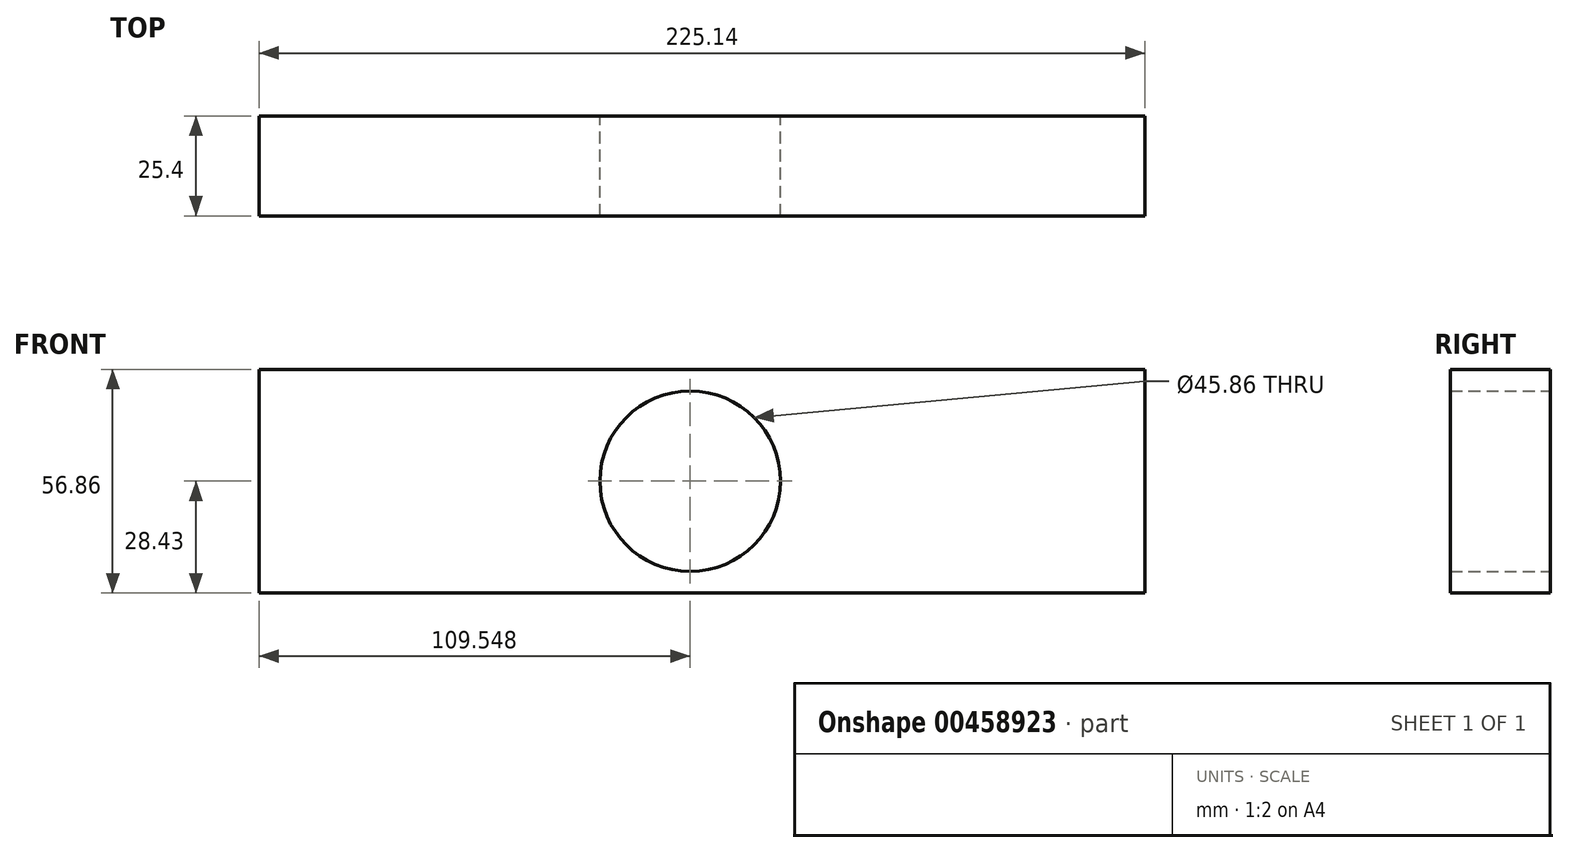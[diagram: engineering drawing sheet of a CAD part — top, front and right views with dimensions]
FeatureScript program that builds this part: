
annotation { "Feature Type Name" : "Feature", "Feature Type Description" : "" }
export const myFeature = defineFeature(function(context is Context, id is Id, definition is map)
    precondition{}
    {
        {
            var Q0;
            Q0=qCreatedBy(makeId("Front.planeOp"),FACE);
            var sketch = newSketch(context, id + "F0", { "sketchPlane" : qUnion([Q0])});
            skLineSegment(sketch, "E0.bottom", {"start": v(-112.57, 28.43) * mm, "end": v(112.57, 28.43) * mm});
            skLineSegment(sketch, "E0.top", {"start": v(-112.57, -28.43) * mm, "end": v(112.57, -28.43) * mm});
            skLineSegment(sketch, "E0.left", {"start": v(-112.57, 28.43) * mm, "end": v(-112.57, -28.43) * mm});
            skLineSegment(sketch, "E0.right", {"start": v(112.57, 28.43) * mm, "end": v(112.57, -28.43) * mm});
            skPoint(sketch, "E0.middle", {"position": v(0, 0) * mm});
            skCircle(sketch, "E1", {"center": v(-3.02, 0) * mm, "radius": 22.93 * mm});
            skSolve(sketch);
        }
        {
            var Q0;
            Q0 = qSketchRegion(id + "F0", true);
            extrude(context, id + "F1", {"entities" : qUnion([Q0]), "depth" : 25.4 * mm});
        }
    });
